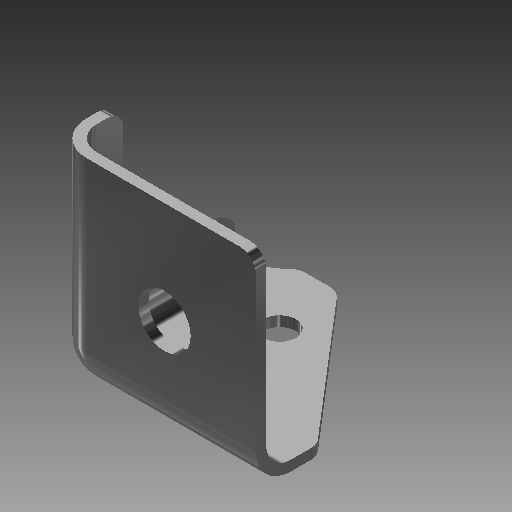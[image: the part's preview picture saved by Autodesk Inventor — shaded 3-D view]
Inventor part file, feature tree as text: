
AUTODESK INVENTOR PART (.ipt)
format: ipt  version: 2019 (Build 230136000, 136)  size: 196,608 bytes
history: native  units: mm
features: sketch x6, extrude x4, projected_geometry x3, fillet x2, hole x2, shell x1
ambient origin geometry x8: Origin, YZ Plane, XZ Plane, XY Plane, X Axis, Y Axis, Z Axis, Center Point
bodies: Solid1 (feature_tree)
feature tree (18):
  extrude  "Extrusion1"  Depth=50.0mm
  fillet  "Fillet1"  Radius=25.0mm
  shell  "Shell1"  Thickness=25.0mm
  extrude  "Extrusion2"  Depth=8.5mm
  extrude  "Extrusion3"  Depth=35.0mm
  hole  "Hole1"  [1 undecoded]
  hole  "Hole2"  [1 undecoded]
  extrude  "Extrusion4"  Depth=35.0mm
  fillet  "Fillet3"  Radius=35.0mm
  sketch  "Sketch1"  dims[d0=50.0mm d1=50.0mm d2=25.0mm d3=25.0mm]
  sketch  "Sketch2"  dims[d4=50.0mm d5=0.0mm d6=8.5mm]
  sketch  "Sketch3"  dims[d7=2.5mm d8=35.0mm]
  sketch  "Sketch4"  dims[d9=35.0mm d10=26.136mm d11=0.0mm]
  projected_geometry  "Projected Loop1"
  projected_geometry  "Projected Loop2"
  sketch  "Sketch5"  dims[d14=26.136mm d15=0.0mm d17=27.606mm]
  projected_geometry  "Projected Loop3"
  sketch  "Sketch6"  dims[d18=25.0mm d19=12.8mm d20=6.0mm d21=4.0mm d22=2.0mm d23=90.0deg d24=8.0mm d25=20.594885mm d28=8.0mm d29=6.0mm d30=4.0mm d31=2.0mm d32=90.0deg d33=8.0mm d34=20.594885mm d36=30.0mm d37=35.0mm d38=2.0mm d39=40.0mm d40=10.0mm d41=0.0mm d42=4.0mm d43=20.785mm d44=35.0mm]
note: 2 required parameter values undecoded (feature->parameter linkage not recoverable at this tier; creation-order binding heuristic only, values carry confidence <= 0.55)
